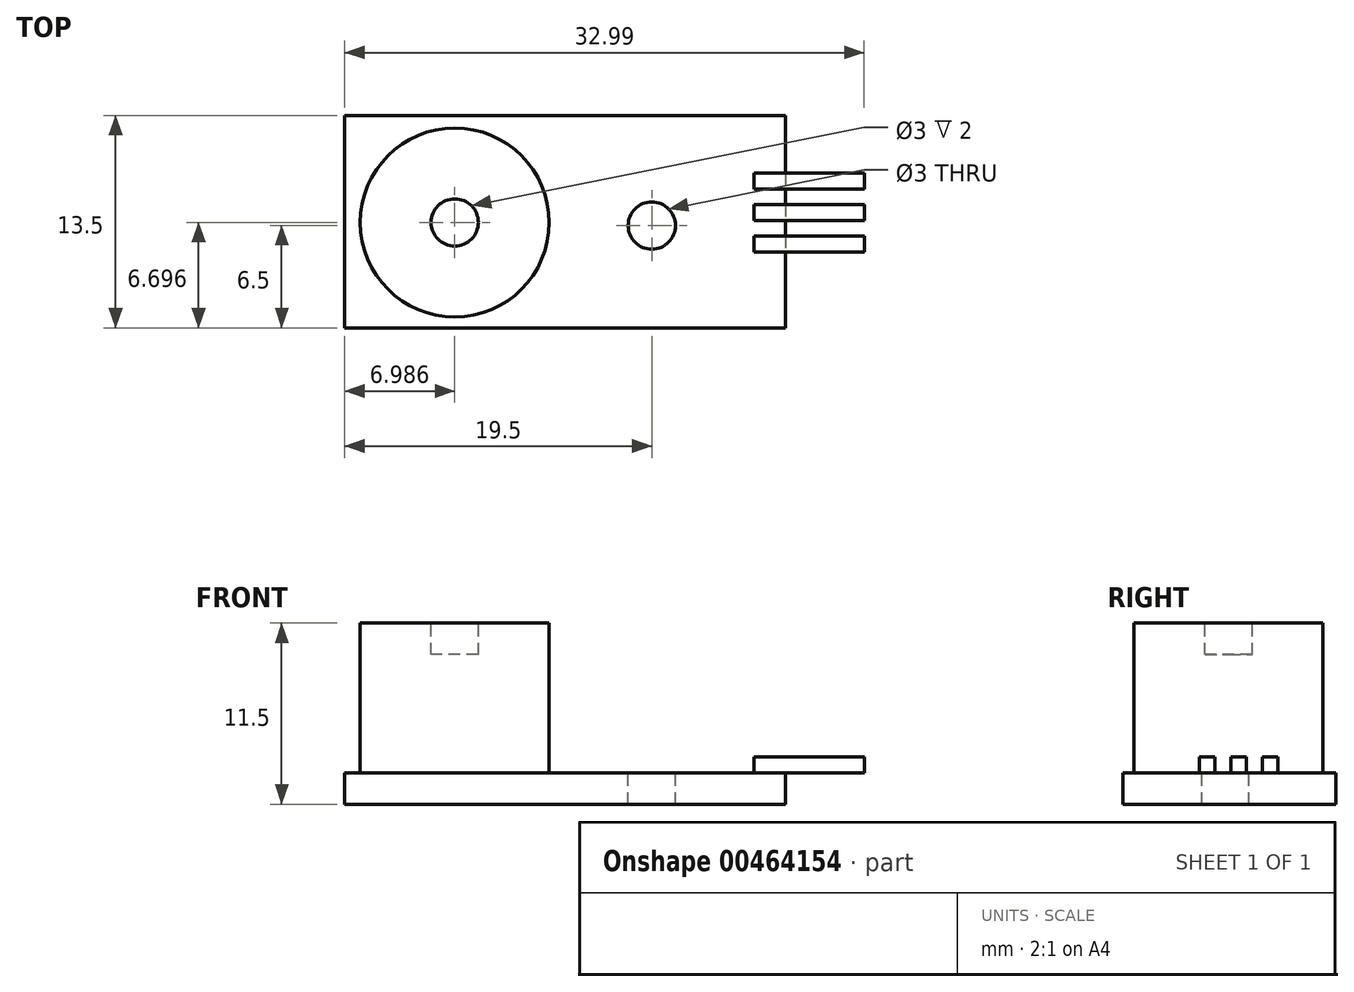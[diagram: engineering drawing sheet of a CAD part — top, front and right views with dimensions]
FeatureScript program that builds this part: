
annotation { "Feature Type Name" : "Feature", "Feature Type Description" : "" }
export const myFeature = defineFeature(function(context is Context, id is Id, definition is map)
    precondition{}
    {
        {
            var Q0;
            Q0=qCreatedBy(makeId("Top.planeOp"),FACE);
            var sketch = newSketch(context, id + "F0", { "sketchPlane" : qUnion([Q0])});
            skLineSegment(sketch, "E0.bottom", {"start": v(0, 0) * mm, "end": v(28, 0) * mm});
            skLineSegment(sketch, "E0.top", {"start": v(0, -13.5) * mm, "end": v(28, -13.5) * mm});
            skLineSegment(sketch, "E0.left", {"start": v(0, 0) * mm, "end": v(0, -13.5) * mm});
            skLineSegment(sketch, "E0.right", {"start": v(28, 0) * mm, "end": v(28, -13.5) * mm});
            skSolve(sketch);
        }
        {
            var Q0;
            Q0 = qSketchRegion(id + "F0", true);
            extrude(context, id + "F1", {"entities" : qUnion([Q0]), "depth" : 2 * mm, "offsetDistance" : 25 * mm});
        }
        {
            var Q0;
            Q0=makeQuery(id+"F1.opExtrude","CAP_FACE",FACE,{"disambiguationData":[OSD([sQuery(id+"F0.wireOp",EDGE,"E0.bottom"),sQuery(id+"F0.wireOp",EDGE,"E0.top"),sQuery(id+"F0.wireOp",EDGE,"E0.left"),sQuery(id+"F0.wireOp",EDGE,"E0.right")])],"isStart":false});
            var sketch = newSketch(context, id + "F2", { "sketchPlane" : qUnion([Q0])});
            skCircle(sketch, "E1", {"center": v(6.99, -6.8) * mm, "radius": 6 * mm});
            skSolve(sketch);
        }
        {
            var Q0;
            Q0 = qSketchRegion(id + "F2", true);
            extrude(context, id + "F3", {"entities" : qUnion([Q0]), "operationType" : NewBodyOperationType.ADD, "depth" : 9.5 * mm, "offsetDistance" : 25 * mm});
        }
        {
            var Q0;
            Q0=makeQuery(id+"F3.opExtrude","CAP_FACE",FACE,{"disambiguationData":[OSD([sQuery(id+"F2.wireOp",EDGE,"E1")])],"isStart":false});
            var sketch = newSketch(context, id + "F4", { "sketchPlane" : qUnion([Q0])});
            skCircle(sketch, "E2", {"center": v(6.99, -6.8) * mm, "radius": 1.5 * mm});
            skSolve(sketch);
        }
        {
            var Q0;
            Q0 = qSketchRegion(id + "F4", true);
            extrude(context, id + "F5", {"entities" : qUnion([Q0]), "operationType" : NewBodyOperationType.REMOVE, "oppositeDirection" : true, "depth" : 2 * mm, "offsetDistance" : 25 * mm});
        }
        {
            var Q0;
            Q0=makeQuery(id+"F1.opExtrude","CAP_FACE",FACE,{"disambiguationData":[OSD([sQuery(id+"F0.wireOp",EDGE,"E0.bottom"),sQuery(id+"F0.wireOp",EDGE,"E0.top"),sQuery(id+"F0.wireOp",EDGE,"E0.left"),sQuery(id+"F0.wireOp",EDGE,"E0.right")])],"isStart":false});
            var sketch = newSketch(context, id + "F6", { "sketchPlane" : qUnion([Q0])});
            skLineSegment(sketch, "E3.bottom", {"start": v(26, -8.67) * mm, "end": v(33, -8.67) * mm});
            skLineSegment(sketch, "E3.top", {"start": v(26, -7.67) * mm, "end": v(33, -7.67) * mm});
            skLineSegment(sketch, "E3.left", {"start": v(26, -8.67) * mm, "end": v(26, -7.67) * mm});
            skLineSegment(sketch, "E3.right", {"start": v(33, -8.67) * mm, "end": v(33, -7.67) * mm});
            skLineSegment(sketch, "E4.bottom", {"start": v(26, -6.67) * mm, "end": v(33, -6.67) * mm});
            skLineSegment(sketch, "E4.top", {"start": v(26, -5.67) * mm, "end": v(33, -5.67) * mm});
            skLineSegment(sketch, "E4.left", {"start": v(26, -6.67) * mm, "end": v(26, -5.67) * mm});
            skLineSegment(sketch, "E4.right", {"start": v(33, -6.67) * mm, "end": v(33, -5.67) * mm});
            skLineSegment(sketch, "E5.bottom", {"start": v(26, -4.67) * mm, "end": v(33, -4.67) * mm});
            skLineSegment(sketch, "E5.top", {"start": v(26, -3.67) * mm, "end": v(33, -3.67) * mm});
            skLineSegment(sketch, "E5.left", {"start": v(26, -4.67) * mm, "end": v(26, -3.67) * mm});
            skLineSegment(sketch, "E5.right", {"start": v(33, -4.67) * mm, "end": v(33, -3.67) * mm});
            skSolve(sketch);
        }
        {
            var Q0;
            Q0 = qSketchRegion(id + "F6", true);
            extrude(context, id + "F7", {"entities" : qUnion([Q0]), "operationType" : NewBodyOperationType.ADD, "depth" : 1 * mm, "offsetDistance" : 25 * mm});
        }
        {
            var Q0;
            Q0=makeQuery(id+"F1.opExtrude","CAP_FACE",FACE,{"disambiguationData":[OSD([sQuery(id+"F0.wireOp",EDGE,"E0.bottom"),sQuery(id+"F0.wireOp",EDGE,"E0.top"),sQuery(id+"F0.wireOp",EDGE,"E0.left"),sQuery(id+"F0.wireOp",EDGE,"E0.right")])],"isStart":false});
            var sketch = newSketch(context, id + "F8", { "sketchPlane" : qUnion([Q0])});
            skCircle(sketch, "E6", {"center": v(19.5, -7) * mm, "radius": 1.5 * mm});
            skSolve(sketch);
        }
        {
            var Q0;
            Q0 = qSketchRegion(id + "F8", true);
            extrude(context, id + "F9", {"entities" : qUnion([Q0]), "operationType" : NewBodyOperationType.REMOVE, "oppositeDirection" : true, "depth" : 25 * mm, "offsetDistance" : 25 * mm});
        }
    });
